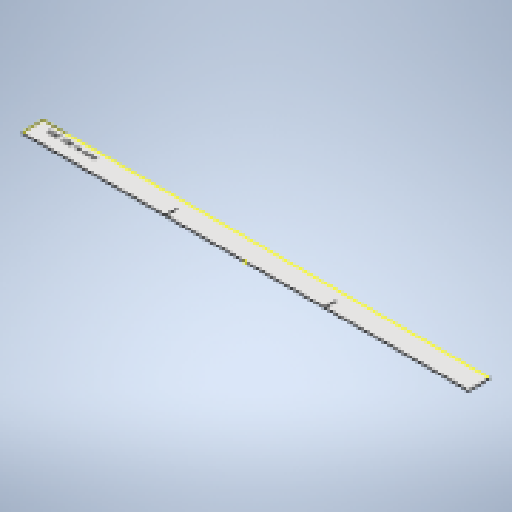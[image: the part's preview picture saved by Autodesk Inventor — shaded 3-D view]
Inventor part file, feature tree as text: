
AUTODESK INVENTOR PART (.ipt)
format: ipt  version: 2025 (Build 290162010, 162A)  size: 257,536 bytes
history: native  units: mm
features: sketch x4, extrude x2, other x2, sheet_metal_op x1, projected_geometry x1
ambient origin geometry x8: Origin, YZ Plane, XZ Plane, XY Plane, X Axis, Y Axis, Z Axis, Center Point
bodies: Body1 (feature_tree)
feature tree (10):
  sheet_metal_op  "Face1"
  extrude  "Extrusion2"  Depth=1200.0mm
  extrude  "Extrusion3"  Depth=50.0mm
  other  "Mark1"
  sketch  "Sketch1"  dims[d18=50.0mm d19=1200.0mm]
  other  "Plate2"
  sketch  "Sketch3"  dims[d20=3.0mm d25=50.0mm]
  sketch  "Sketch4"  dims[d26=50.0mm]
  projected_geometry  "Projected Loop1"
  sketch  "Sketch5"  dims[d28=3.0mm d29=26.0mm d30=0.0mm d31=0.0mm d35=190.0mm d36=190.0mm d37=3.0mm d38=26.0mm d39=12.217305mm d40=35.0mm d45=67.0mm d46=67.0mm d47=0.0mm d48=0.0mm]
